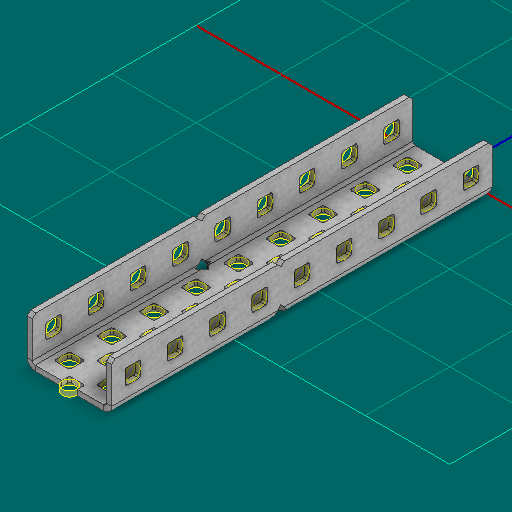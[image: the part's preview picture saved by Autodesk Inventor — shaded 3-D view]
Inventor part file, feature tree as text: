
AUTODESK INVENTOR PART (.ipt)
format: ipt  version: 2025 (Build 290162000, 162)  size: 923,648 bytes
history: native  units: in
note: dims shown in document units (in); Inventor stores cm internally (conversion verified against a paired STEP export)
features: other x96, sketch x5, sheet_metal_op x1
ambient origin geometry x8: Origin, YZ Plane, XZ Plane, XY Plane, X Axis, Y Axis, Z Axis, Center Point
bodies: Solid1 (feature_tree)
feature tree (102):
  other  "Alu C 1x2x1x9.ipt"
  other  "Solid1::Alu C 1x2x1x9.ipt"
  other  "TaggingFeature1"
  sketch  "Sketch1"  dims[d0=0.3937in]
  sketch  "Sketch2"  dims[d1=0.0625in]
  sketch  "Sketch3"
  other  "Flange Pattern Sketch"
  sketch  "Sketch9"
  sheet_metal_op  "Body Pattern Sketch"
  other  "Arc Length"
  sketch  "Sketch14"
  other  "Flange Pattern Plane"
  other  "Srf1"
  other  "Srf2"
  other  "Srf3"
  other  "Srf4"
  other  "Srf5"
  other  "Srf6"
  other  "Srf7"
  other  "Srf8"
  other  "Srf9"
  other  "Srf10"
  other  "Srf11"
  other  "Srf12"
  other  "Srf13"
  other  "Srf14"
  other  "Srf15"
  other  "Srf16"
  other  "Srf17"
  other  "Srf18"
  other  "Srf19"
  other  "Srf20"
  other  "Srf21"
  other  "Srf22"
  other  "Srf23"
  other  "Srf24"
  other  "Srf25"
  other  "Srf26"
  other  "Srf27"
  other  "Srf28"
  other  "Srf29"
  other  "Srf30"
  other  "Srf31"
  other  "Srf32"
  other  "Srf33"
  other  "Srf34"
  other  "Srf35"
  other  "Srf36"
  other  "Srf37"
  other  "Srf38"
  other  "Srf39"
  other  "Srf40"
  other  "Srf41"
  other  "Srf42"
  other  "Srf43"
  other  "Srf44"
  other  "Srf45"
  other  "Srf1::Derived"
  other  "Srf2::Derived"
  other  "Srf823::Derived"
  other  "Srf824::Derived"
  other  "Srf825::Derived"
  other  "Srf826::Derived"
  other  "Srf827::Derived"
  other  "Srf828::Derived"
  other  "Srf829::Derived"
  other  "Srf922::Derived"
  other  "Srf923::Derived"
  other  "Srf924::Derived"
  other  "Srf925::Derived"
  other  "Srf926::Derived"
  other  "Srf1143::Derived"
  other  "Srf1144::Derived"
  other  "Srf1145::Derived"
  other  "Srf1146::Derived"
  other  "Srf91::Derived"
  other  "Srf92::Derived"
  other  "Srf856::Derived"
  other  "Srf857::Derived"
  other  "Srf858::Derived"
  other  "Srf859::Derived"
  other  "Srf860::Derived"
  other  "Srf861::Derived"
  other  "Srf862::Derived"
  other  "Srf959::Derived"
  other  "Srf960::Derived"
  other  "Srf961::Derived"
  other  "Srf962::Derived"
  other  "Srf963::Derived"
  other  "Srf1199::Derived"
  other  "Srf1200::Derived"
  other  "Srf1201::Derived"
  other  "Srf1202::Derived"
  other  "Srf786::Derived"
  other  "Srf889::Derived"
  other  "Srf890::Derived"
  other  "Srf891::Derived"
  other  "Srf892::Derived"
  other  "Srf893::Derived"
  other  "Srf894::Derived"
  other  "Srf895::Derived"
  other  "Srf896::Derived"
